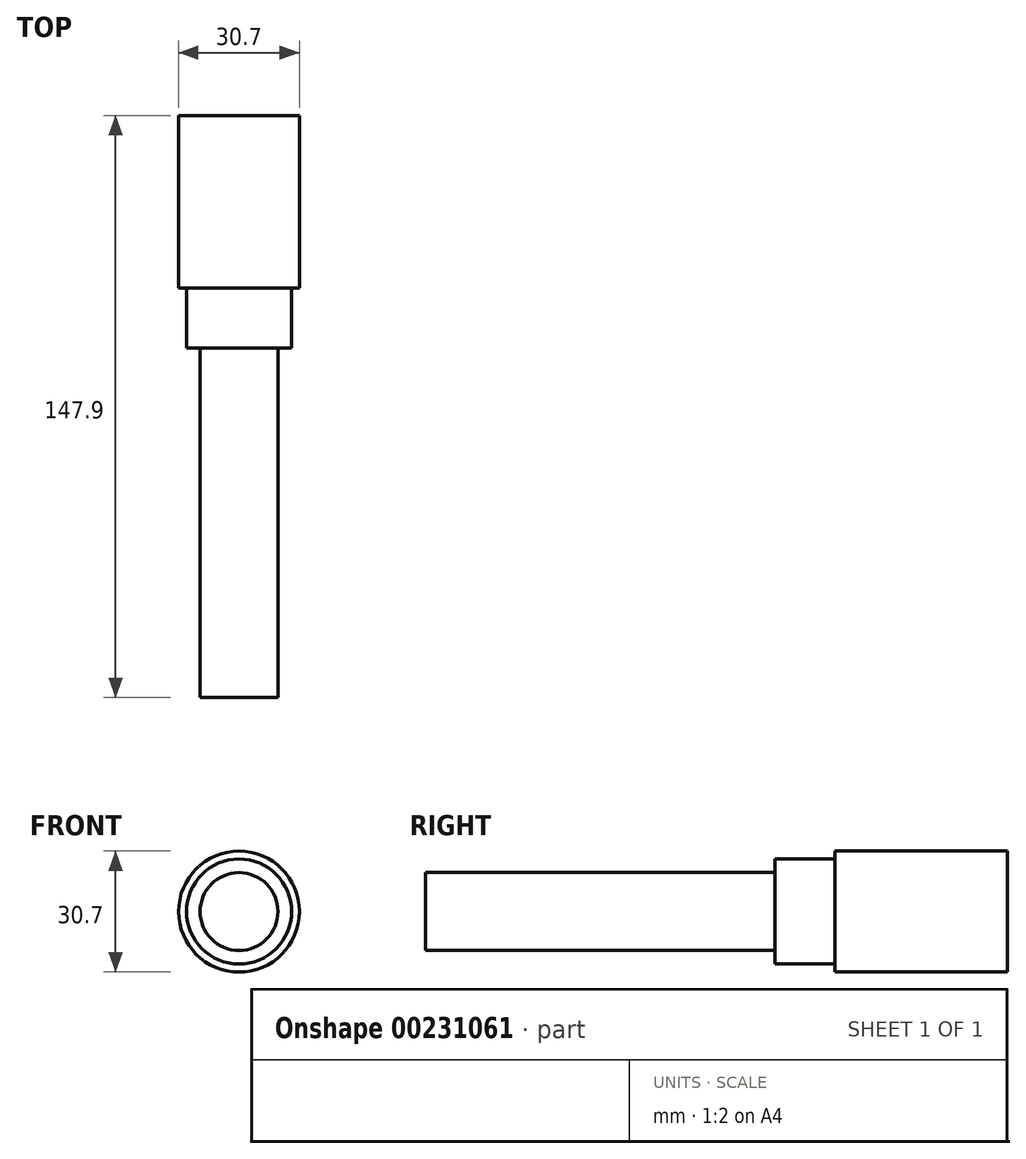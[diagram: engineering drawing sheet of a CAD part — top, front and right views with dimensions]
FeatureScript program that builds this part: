
annotation { "Feature Type Name" : "Feature", "Feature Type Description" : "" }
export const myFeature = defineFeature(function(context is Context, id is Id, definition is map)
    precondition{}
    {
        {
            var Q0;
            Q0=qCreatedBy(makeId("Front.planeOp"),FACE);
            var sketch = newSketch(context, id + "F0", { "sketchPlane" : qUnion([Q0])});
            skCircle(sketch, "E0", {"center": v(0, 0) * mm, "radius": 15.35 * mm});
            skSolve(sketch);
        }
        {
            var Q0;
            Q0 = qSketchRegion(id + "F0", true);
            extrude(context, id + "F1", {"entities" : qUnion([Q0]), "depth" : 43.88 * mm});
        }
        {
            var Q0;
            Q0=makeQuery(id+"F1.opExtrude","CAP_FACE",FACE,{"disambiguationData":[OSD([sQuery(id+"F0.wireOp",EDGE,"E0")])],"isStart":false});
            var sketch = newSketch(context, id + "F2", { "sketchPlane" : qUnion([Q0])});
            skCircle(sketch, "E1", {"center": v(0, 0) * mm, "radius": 13.35 * mm});
            skSolve(sketch);
        }
        {
            var Q0;
            Q0=makeQuery(id+"F2.imprint","IMPRINT",FACE,{"disambiguationData":[TD([[makeQuery(id+"F2.imprint","IMPRINT",EDGE,{"derivedFrom":sQuery(id+"F2.wireOp",EDGE,"E1")}),1.0]])]});
            extrude(context, id + "F3", {"entities" : qUnion([Q0]), "operationType" : NewBodyOperationType.ADD, "depth" : 15.24 * mm});
        }
        {
            var Q0;
            Q0=makeQuery(id+"F3.opExtrude","CAP_FACE",FACE,{"disambiguationData":[OSD([sQuery(id+"F2.wireOp",EDGE,"E1")])],"isStart":false});
            var sketch = newSketch(context, id + "F4", { "sketchPlane" : qUnion([Q0])});
            skCircle(sketch, "E2", {"center": v(0, 0) * mm, "radius": 9.9 * mm});
            skSolve(sketch);
        }
        {
            var Q0;
            Q0 = qSketchRegion(id + "F4", true);
            extrude(context, id + "F5", {"entities" : qUnion([Q0]), "operationType" : NewBodyOperationType.ADD, "depth" : 88.78 * mm});
        }
    });
